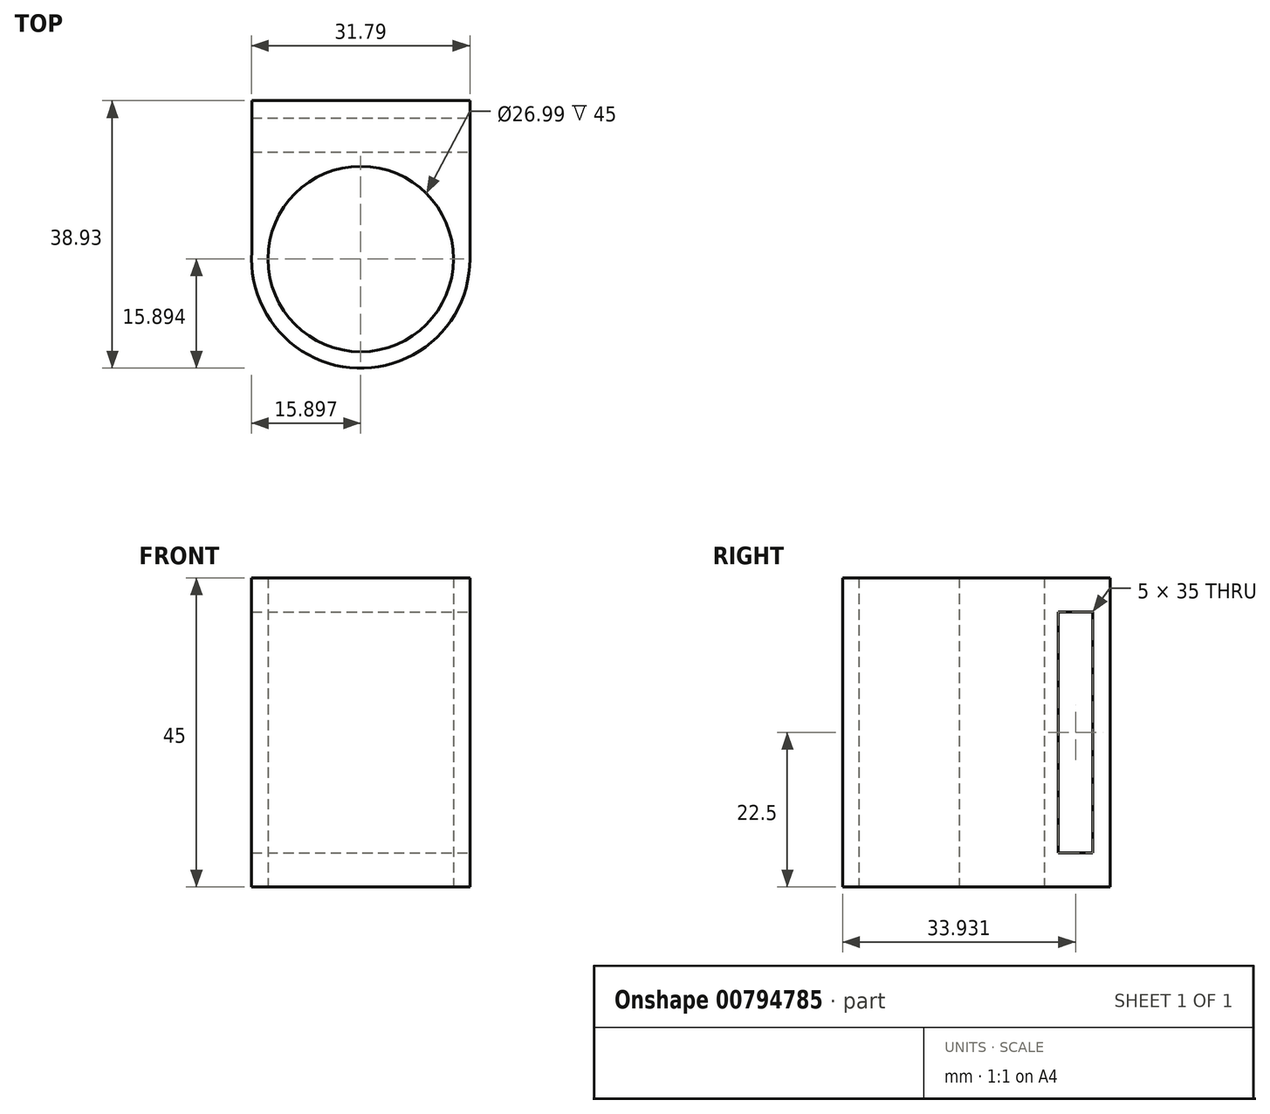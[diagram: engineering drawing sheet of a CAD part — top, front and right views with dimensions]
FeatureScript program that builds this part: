
annotation { "Feature Type Name" : "Feature", "Feature Type Description" : "" }
export const myFeature = defineFeature(function(context is Context, id is Id, definition is map)
    precondition{}
    {
        {
            var Q0;
            Q0=qCreatedBy(makeId("Top.planeOp"),FACE);
            var sketch = newSketch(context, id + "F0", { "sketchPlane" : qUnion([Q0])});
            skLineSegment(sketch, "E0.bottom", {"start": v(-17.7, 12.7) * mm, "end": v(14.05, 12.7) * mm});
            skLineSegment(sketch, "E0.left", {"start": v(-17.7, 12.7) * mm, "end": v(-17.7, -10.36) * mm});
            skLineSegment(sketch, "E0.right", {"start": v(14.05, 12.7) * mm, "end": v(14.05, -10.36) * mm});
            skCircle(sketch, "E1", {"center": v(-1.84, -10.34) * mm, "radius": 13.5 * mm});
            skArc(sketch, "E2", {"start": v(-17.7, -9.24) * mm, "mid": v(-2.38, -26.22) * mm, "end": v(14.05, -10.32) * mm});
            skSolve(sketch);
        }
        {
            var Q0;
            Q0 = qSketchRegion(id + "F0", true);
            extrude(context, id + "F1", {"entities" : qUnion([Q0]), "depth" : 45 * mm, "offsetDistance" : 25.4 * mm});
        }
        {
            var Q0;
            Q0=makeQuery(id+"F1.opExtrude","SWEPT_FACE",FACE,{"disambiguationData":[OSD([sQuery(id+"F0.wireOp",EDGE,"E0.right")])]});
            var sketch = newSketch(context, id + "F2", { "sketchPlane" : qUnion([Q0])});
            skLineSegment(sketch, "E3.bottom", {"start": v(10.2, 40) * mm, "end": v(5.2, 40) * mm});
            skLineSegment(sketch, "E3.top", {"start": v(10.2, 5) * mm, "end": v(5.2, 5) * mm});
            skLineSegment(sketch, "E3.left", {"start": v(10.2, 40) * mm, "end": v(10.2, 5) * mm});
            skLineSegment(sketch, "E3.right", {"start": v(5.2, 40) * mm, "end": v(5.2, 5) * mm});
            skSolve(sketch);
        }
        {
            var Q0;
            Q0 = qSketchRegion(id + "F2", true);
            extrude(context, id + "F3", {"entities" : qUnion([Q0]), "operationType" : NewBodyOperationType.REMOVE, "oppositeDirection" : true, "depth" : 33.8 * mm, "offsetDistance" : 25.4 * mm});
        }
    });
